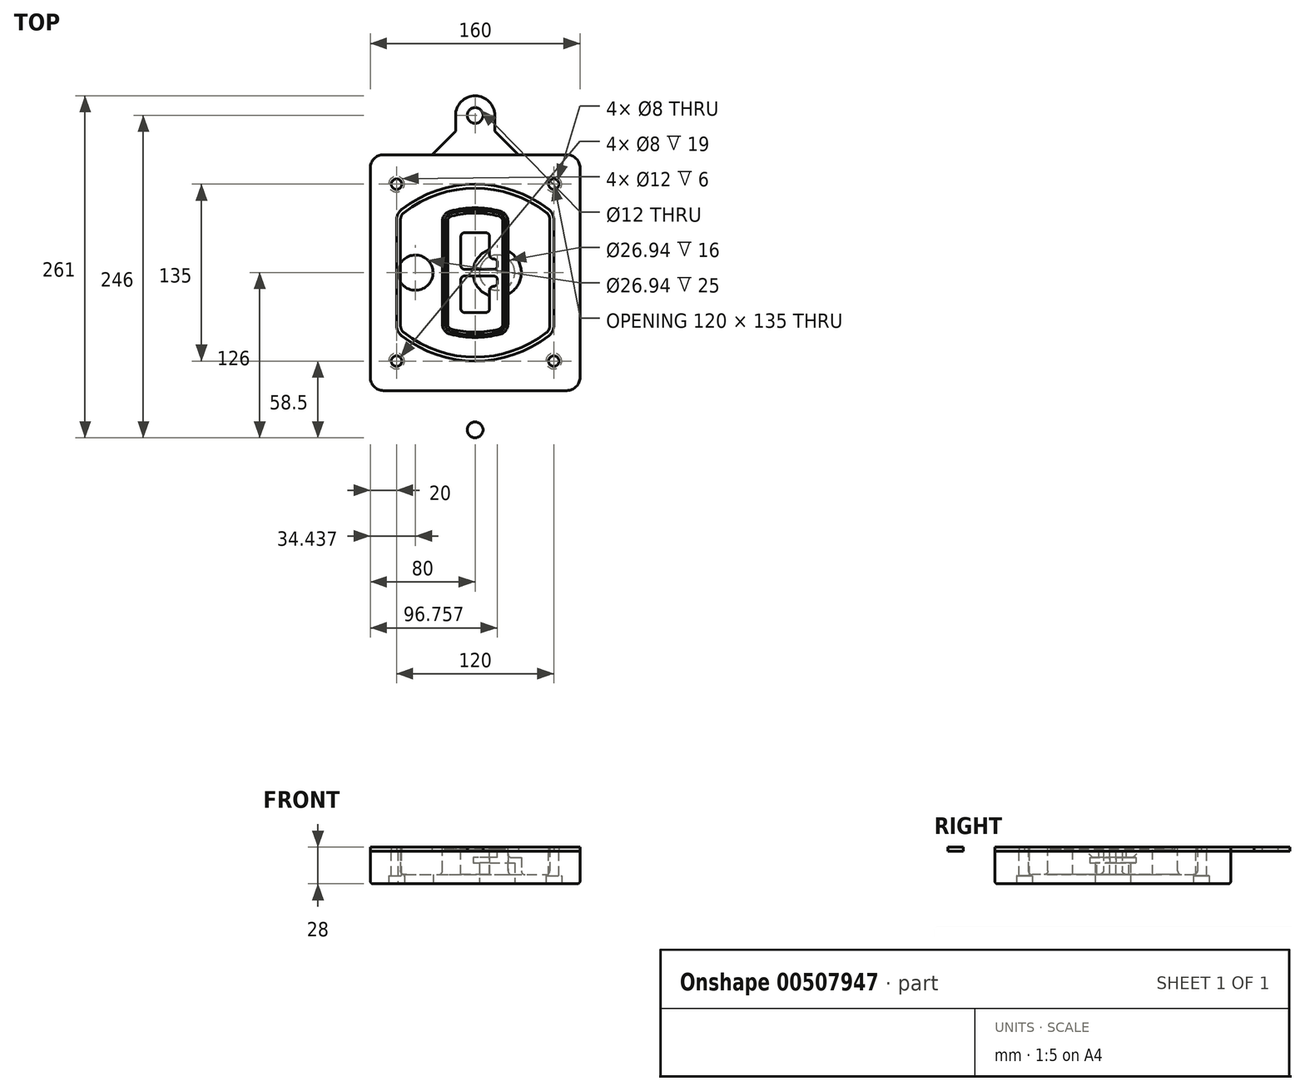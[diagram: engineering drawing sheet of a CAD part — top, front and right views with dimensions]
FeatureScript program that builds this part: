
annotation { "Feature Type Name" : "Feature", "Feature Type Description" : "" }
export const myFeature = defineFeature(function(context is Context, id is Id, definition is map)
    precondition{}
    {
        {
            var Q0;
            Q0=qCreatedBy(makeId("Top.planeOp"),FACE);
            var sketch = newSketch(context, id + "F0", { "sketchPlane" : qUnion([Q0])});
            skPoint(sketch, "E0.rect.middle", {"position": v(0, 0) * mm});
            skLineSegment(sketch, "E1.bottom", {"start": v(-70, -90) * mm, "end": v(70, -90) * mm});
            skLineSegment(sketch, "E1.top", {"start": v(-70, 90) * mm, "end": v(70, 90) * mm});
            skLineSegment(sketch, "E1.left", {"start": v(-80, -80) * mm, "end": v(-80, 80) * mm});
            skLineSegment(sketch, "E1.right", {"start": v(80, -80) * mm, "end": v(80, 80) * mm});
            skLineSegment(sketch, "E2", {"start": v(-80, 90) * mm, "end": v(80, -90) * mm, "construction": true});
            skLineSegment(sketch, "E3", {"start": v(80, 90) * mm, "end": v(-80, -90) * mm, "construction": true});
            skCircle(sketch, "E4", {"center": v(-60, 67.5) * mm, "radius": 4 * mm});
            skCircle(sketch, "E5", {"center": v(60, 67.5) * mm, "radius": 4 * mm});
            skCircle(sketch, "E6", {"center": v(60, -67.5) * mm, "radius": 4 * mm});
            skCircle(sketch, "E7", {"center": v(-60, -67.5) * mm, "radius": 4 * mm});
            skLineSegment(sketch, "E8", {"start": v(-60, 67.5) * mm, "end": v(60, 67.5) * mm, "construction": true});
            skLineSegment(sketch, "E9", {"start": v(60, 67.5) * mm, "end": v(60, -67.5) * mm, "construction": true});
            skLineSegment(sketch, "E10", {"start": v(60, -67.5) * mm, "end": v(-60, -67.5) * mm, "construction": true});
            skLineSegment(sketch, "E11", {"start": v(-60, -67.5) * mm, "end": v(-60, 67.5) * mm, "construction": true});
            skLineSegment(sketch, "E12", {"start": v(-60, 40.3) * mm, "end": v(-60, -40.3) * mm});
            skLineSegment(sketch, "E13", {"start": v(60, 40.3) * mm, "end": v(60, -40.3) * mm});
            skArc(sketch, "E14", {"start": v(56.15, 48.18) * mm, "mid": v(0, 67.5) * mm, "end": v(-56.15, 48.18) * mm});
            skArc(sketch, "E15", {"start": v(-56.15, -48.18) * mm, "mid": v(0, -67.5) * mm, "end": v(56.15, -48.18) * mm});
            skLineSegment(sketch, "E16", {"start": v(-60, 0) * mm, "end": v(60, 0) * mm, "construction": true});
            skPoint(sketch, "E17.visualSharp", {"position": v(-60, -45) * mm});
            skArc(sketch, "E17.filletArc", {"start": v(-60, -40.3) * mm, "mid": v(-58.99, -44.68) * mm, "end": v(-56.15, -48.18) * mm});
            skPoint(sketch, "E18.visualSharp", {"position": v(-60, 45) * mm});
            skArc(sketch, "E18.filletArc", {"start": v(-56.15, 48.18) * mm, "mid": v(-58.99, 44.68) * mm, "end": v(-60, 40.3) * mm});
            skPoint(sketch, "E19.visualSharp", {"position": v(60, 45) * mm});
            skArc(sketch, "E19.filletArc", {"start": v(60, 40.3) * mm, "mid": v(58.99, 44.68) * mm, "end": v(56.15, 48.18) * mm});
            skPoint(sketch, "E20.visualSharp", {"position": v(60, -45) * mm});
            skArc(sketch, "E20.filletArc", {"start": v(56.15, -48.18) * mm, "mid": v(58.99, -44.68) * mm, "end": v(60, -40.3) * mm});
            skPoint(sketch, "E21.visualSharp", {"position": v(-80, 90) * mm});
            skArc(sketch, "E21.filletArc", {"start": v(-70, 90) * mm, "mid": v(-77.07, 87.07) * mm, "end": v(-80, 80) * mm});
            skPoint(sketch, "E22.visualSharp", {"position": v(80, 90) * mm});
            skArc(sketch, "E22.filletArc", {"start": v(80, 80) * mm, "mid": v(77.07, 87.07) * mm, "end": v(70, 90) * mm});
            skPoint(sketch, "E23.visualSharp", {"position": v(80, -90) * mm});
            skArc(sketch, "E23.filletArc", {"start": v(70, -90) * mm, "mid": v(77.07, -87.07) * mm, "end": v(80, -80) * mm});
            skPoint(sketch, "E24.visualSharp", {"position": v(-80, -90) * mm});
            skArc(sketch, "E24.filletArc", {"start": v(-80, -80) * mm, "mid": v(-77.07, -87.07) * mm, "end": v(-70, -90) * mm});
            skArc(sketch, "E25.0", {"start": v(57, 40.3) * mm, "mid": v(56.3, 43.36) * mm, "end": v(54.3, 45.81) * mm});
            skLineSegment(sketch, "E25.1", {"start": v(57, 40.3) * mm, "end": v(57, -40.3) * mm});
            skArc(sketch, "E25.2", {"start": v(54.3, -45.81) * mm, "mid": v(56.3, -43.36) * mm, "end": v(57, -40.3) * mm});
            skArc(sketch, "E25.3", {"start": v(-54.3, -45.81) * mm, "mid": v(0, -64.5) * mm, "end": v(54.3, -45.81) * mm});
            skArc(sketch, "E25.4", {"start": v(-57, -40.3) * mm, "mid": v(-56.3, -43.36) * mm, "end": v(-54.3, -45.81) * mm});
            skArc(sketch, "E25.5", {"start": v(54.3, 45.81) * mm, "mid": v(0, 64.5) * mm, "end": v(-54.3, 45.81) * mm});
            skLineSegment(sketch, "E25.6", {"start": v(-57, 40.3) * mm, "end": v(-57, -40.3) * mm});
            skArc(sketch, "E25.7", {"start": v(-54.3, 45.81) * mm, "mid": v(-56.3, 43.36) * mm, "end": v(-57, 40.3) * mm});
            skArc(sketch, "E26.0", {"start": v(-58.62, 51.33) * mm, "mid": v(-62.58, 46.43) * mm, "end": v(-64, 40.3) * mm});
            skArc(sketch, "E26.1", {"start": v(58.62, 51.33) * mm, "mid": v(0, 71.5) * mm, "end": v(-58.62, 51.33) * mm});
            skArc(sketch, "E26.2", {"start": v(64, 40.3) * mm, "mid": v(62.58, 46.43) * mm, "end": v(58.62, 51.33) * mm});
            skLineSegment(sketch, "E26.3", {"start": v(64, 40.3) * mm, "end": v(64, -40.3) * mm});
            skArc(sketch, "E26.4", {"start": v(58.62, -51.33) * mm, "mid": v(62.58, -46.43) * mm, "end": v(64, -40.3) * mm});
            skLineSegment(sketch, "E26.5", {"start": v(-64, 40.3) * mm, "end": v(-64, -40.3) * mm});
            skArc(sketch, "E26.6", {"start": v(-58.62, -51.33) * mm, "mid": v(0, -71.5) * mm, "end": v(58.62, -51.33) * mm});
            skArc(sketch, "E26.7", {"start": v(-64, -40.3) * mm, "mid": v(-62.58, -46.43) * mm, "end": v(-58.62, -51.33) * mm});
            skSolve(sketch);
        }
        {
            var Q0;
            Q0=makeQuery(id+"F0.imprint","IMPRINT",FACE,{"disambiguationData":[TD([[makeQuery(id+"F0.imprint","IMPRINT",EDGE,{"derivedFrom":sQuery(id+"F0.wireOp",EDGE,"E1.bottom")}),1.0]])]});
            var Q1;
            Q1=makeQuery(id+"F0.imprint","IMPRINT",FACE,{"disambiguationData":[TD([[makeQuery(id+"F0.imprint","IMPRINT",EDGE,{"derivedFrom":sQuery(id+"F0.wireOp",EDGE,"E12")}),1.0]])]});
            var Q2;
            Q2=makeQuery(id+"F0.imprint","IMPRINT",FACE,{"disambiguationData":[TD([[makeQuery(id+"F0.imprint","IMPRINT",EDGE,{"derivedFrom":sQuery(id+"F0.wireOp",EDGE,"E25.0")}),1.0]])]});
            var Q3;
            Q3=makeQuery(id+"F0.imprint","IMPRINT",FACE,{"disambiguationData":[TD([[makeQuery(id+"F0.imprint","IMPRINT",EDGE,{"derivedFrom":sQuery(id+"F0.wireOp",EDGE,"E12")}),-1.0]])]});
            extrude(context, id + "F1", {"entities" : qUnion([Q0, Q1, Q2, Q3]), "oppositeDirection" : true, "depth" : 25 * mm});
        }
        {
            var Q0;
            Q0=makeQuery(id+"F0.imprint","IMPRINT",FACE,{"disambiguationData":[TD([[makeQuery(id+"F0.imprint","IMPRINT",EDGE,{"derivedFrom":sQuery(id+"F0.wireOp",EDGE,"E12")}),1.0]])]});
            extrude(context, id + "F2", {"entities" : qUnion([Q0]), "operationType" : NewBodyOperationType.ADD, "depth" : 3 * mm});
        }
        {
            var Q0;
            Q0=makeQuery(id+"F0.imprint","IMPRINT",FACE,{"disambiguationData":[TD([[makeQuery(id+"F0.imprint","IMPRINT",EDGE,{"derivedFrom":sQuery(id+"F0.wireOp",EDGE,"E25.0")}),1.0]])]});
            extrude(context, id + "F3", {"entities" : qUnion([Q0]), "operationType" : NewBodyOperationType.REMOVE, "oppositeDirection" : true, "depth" : 18 * mm});
        }
        {
            var Q0;
            Q0=makeQuery(id+"F2.opExtrude","CAP_FACE",FACE,{"disambiguationData":[OSD([sQuery(id+"F0.wireOp",EDGE,"E12"),sQuery(id+"F0.wireOp",EDGE,"E13"),sQuery(id+"F0.wireOp",EDGE,"E14"),sQuery(id+"F0.wireOp",EDGE,"E15"),sQuery(id+"F0.wireOp",EDGE,"E17.filletArc"),sQuery(id+"F0.wireOp",EDGE,"E18.filletArc"),sQuery(id+"F0.wireOp",EDGE,"E19.filletArc"),sQuery(id+"F0.wireOp",EDGE,"E20.filletArc"),sQuery(id+"F0.wireOp",EDGE,"E25.0"),sQuery(id+"F0.wireOp",EDGE,"E25.1"),sQuery(id+"F0.wireOp",EDGE,"E25.2"),sQuery(id+"F0.wireOp",EDGE,"E25.3"),sQuery(id+"F0.wireOp",EDGE,"E25.4"),sQuery(id+"F0.wireOp",EDGE,"E25.5"),sQuery(id+"F0.wireOp",EDGE,"E25.6"),sQuery(id+"F0.wireOp",EDGE,"E25.7")])],"isStart":false});
            var sketch = newSketch(context, id + "F4", { "sketchPlane" : qUnion([Q0])});
            skArc(sketch, "E27.0", {"start": v(-19.08, -46.97) * mm, "mid": v(0, -49.5) * mm, "end": v(19.08, -46.97) * mm});
            skArc(sketch, "E28.0", {"start": v(19.08, 46.97) * mm, "mid": v(0, 49.5) * mm, "end": v(-19.08, 46.97) * mm});
            skLineSegment(sketch, "E29", {"start": v(-25, 39.25) * mm, "end": v(-25, -39.25) * mm});
            skLineSegment(sketch, "E30", {"start": v(25, 39.25) * mm, "end": v(25, -39.25) * mm});
            skLineSegment(sketch, "E31", {"start": v(-25, 45.1) * mm, "end": v(25, 45.1) * mm, "construction": true});
            skLineSegment(sketch, "E32", {"start": v(-25, -45.1) * mm, "end": v(25, -45.1) * mm, "construction": true});
            skPoint(sketch, "E33.visualSharp", {"position": v(-25, 45.1) * mm});
            skArc(sketch, "E33.filletArc", {"start": v(-19.08, 46.97) * mm, "mid": v(-23.35, 44.11) * mm, "end": v(-25, 39.25) * mm});
            skPoint(sketch, "E34.visualSharp", {"position": v(25, 45.1) * mm});
            skArc(sketch, "E34.filletArc", {"start": v(25, 39.25) * mm, "mid": v(23.35, 44.11) * mm, "end": v(19.08, 46.97) * mm});
            skPoint(sketch, "E35.visualSharp", {"position": v(25, -45.1) * mm});
            skArc(sketch, "E35.filletArc", {"start": v(19.08, -46.97) * mm, "mid": v(23.35, -44.11) * mm, "end": v(25, -39.25) * mm});
            skPoint(sketch, "E36.visualSharp", {"position": v(-25, -45.1) * mm});
            skArc(sketch, "E36.filletArc", {"start": v(-25, -39.25) * mm, "mid": v(-23.35, -44.11) * mm, "end": v(-19.08, -46.97) * mm});
            skArc(sketch, "E37.0", {"start": v(54.3, 45.81) * mm, "mid": v(0, 64.5) * mm, "end": v(-54.3, 45.81) * mm});
            skArc(sketch, "E37.1", {"start": v(-54.3, 45.81) * mm, "mid": v(-56.3, 43.36) * mm, "end": v(-57, 40.3) * mm});
            skLineSegment(sketch, "E37.2", {"start": v(-57, 40.3) * mm, "end": v(-57, -40.3) * mm});
            skArc(sketch, "E37.3", {"start": v(-57, -40.3) * mm, "mid": v(-56.3, -43.36) * mm, "end": v(-54.3, -45.81) * mm});
            skArc(sketch, "E37.4", {"start": v(-54.3, -45.81) * mm, "mid": v(0, -64.5) * mm, "end": v(54.3, -45.81) * mm});
            skArc(sketch, "E37.5", {"start": v(54.3, -45.81) * mm, "mid": v(56.3, -43.36) * mm, "end": v(57, -40.3) * mm});
            skLineSegment(sketch, "E37.6", {"start": v(57, 40.3) * mm, "end": v(57, -40.3) * mm});
            skArc(sketch, "E37.7", {"start": v(57, 40.3) * mm, "mid": v(56.3, 43.36) * mm, "end": v(54.3, 45.81) * mm});
            skLineSegment(sketch, "E38.0", {"start": v(23, 39.25) * mm, "end": v(23, -39.25) * mm});
            skArc(sketch, "E38.1", {"start": v(18.56, -45.04) * mm, "mid": v(21.76, -42.9) * mm, "end": v(23, -39.25) * mm});
            skArc(sketch, "E38.2", {"start": v(-18.56, -45.04) * mm, "mid": v(0, -47.5) * mm, "end": v(18.56, -45.04) * mm});
            skArc(sketch, "E38.3", {"start": v(-23, -39.25) * mm, "mid": v(-21.76, -42.9) * mm, "end": v(-18.56, -45.04) * mm});
            skLineSegment(sketch, "E38.4", {"start": v(-23, 39.25) * mm, "end": v(-23, -39.25) * mm});
            skArc(sketch, "E38.5", {"start": v(23, 39.25) * mm, "mid": v(21.76, 42.9) * mm, "end": v(18.56, 45.04) * mm});
            skArc(sketch, "E38.6", {"start": v(-18.56, 45.04) * mm, "mid": v(-21.76, 42.9) * mm, "end": v(-23, 39.25) * mm});
            skArc(sketch, "E38.7", {"start": v(18.56, 45.04) * mm, "mid": v(0, 47.5) * mm, "end": v(-18.56, 45.04) * mm});
            skArc(sketch, "E39.0", {"start": v(21, 39.25) * mm, "mid": v(20.18, 41.68) * mm, "end": v(18.04, 43.1) * mm});
            skLineSegment(sketch, "E39.1", {"start": v(21, 39.25) * mm, "end": v(21, -39.25) * mm});
            skArc(sketch, "E39.2", {"start": v(18.04, -43.1) * mm, "mid": v(20.18, -41.68) * mm, "end": v(21, -39.25) * mm});
            skArc(sketch, "E39.3", {"start": v(-18.04, -43.1) * mm, "mid": v(0, -45.5) * mm, "end": v(18.04, -43.1) * mm});
            skArc(sketch, "E39.4", {"start": v(-21, -39.25) * mm, "mid": v(-20.18, -41.68) * mm, "end": v(-18.04, -43.1) * mm});
            skArc(sketch, "E39.5", {"start": v(18.04, 43.1) * mm, "mid": v(0, 45.5) * mm, "end": v(-18.04, 43.1) * mm});
            skLineSegment(sketch, "E39.6", {"start": v(-21, 39.25) * mm, "end": v(-21, -39.25) * mm});
            skArc(sketch, "E39.7", {"start": v(-18.04, 43.1) * mm, "mid": v(-20.18, 41.68) * mm, "end": v(-21, 39.25) * mm});
            skLineSegment(sketch, "E40", {"start": v(-25, 0) * mm, "end": v(25, 0) * mm, "construction": true});
            skLineSegment(sketch, "E41", {"start": v(-11, 5.5) * mm, "end": v(-11, 27.5) * mm});
            skLineSegment(sketch, "E42", {"start": v(-8, 30.5) * mm, "end": v(8, 30.5) * mm});
            skLineSegment(sketch, "E43", {"start": v(11, 27.5) * mm, "end": v(11, 13.5) * mm});
            skLineSegment(sketch, "E44", {"start": v(14, 10.5) * mm, "end": v(14, 10.5) * mm});
            skLineSegment(sketch, "E45", {"start": v(17, 7.5) * mm, "end": v(17, 5.5) * mm});
            skLineSegment(sketch, "E46", {"start": v(14, 2.5) * mm, "end": v(-8, 2.5) * mm});
            skPoint(sketch, "E47.visualSharp", {"position": v(-11, 30.5) * mm});
            skArc(sketch, "E47.filletArc", {"start": v(-8, 30.5) * mm, "mid": v(-10.12, 29.62) * mm, "end": v(-11, 27.5) * mm});
            skPoint(sketch, "E48.visualSharp", {"position": v(11, 30.5) * mm});
            skArc(sketch, "E48.filletArc", {"start": v(11, 27.5) * mm, "mid": v(10.12, 29.62) * mm, "end": v(8, 30.5) * mm});
            skPoint(sketch, "E49.visualSharp", {"position": v(11, 10.5) * mm});
            skArc(sketch, "E49.filletArc", {"start": v(11, 13.5) * mm, "mid": v(11.88, 11.38) * mm, "end": v(14, 10.5) * mm});
            skPoint(sketch, "E50.visualSharp", {"position": v(17, 10.5) * mm});
            skArc(sketch, "E50.filletArc", {"start": v(17, 7.5) * mm, "mid": v(16.12, 9.62) * mm, "end": v(14, 10.5) * mm});
            skPoint(sketch, "E51.visualSharp", {"position": v(17, 2.5) * mm});
            skArc(sketch, "E51.filletArc", {"start": v(14, 2.5) * mm, "mid": v(16.12, 3.38) * mm, "end": v(17, 5.5) * mm});
            skPoint(sketch, "E52.visualSharp", {"position": v(-11, 2.5) * mm});
            skArc(sketch, "E52.filletArc", {"start": v(-11, 5.5) * mm, "mid": v(-10.12, 3.38) * mm, "end": v(-8, 2.5) * mm});
            skLineSegment(sketch, "E53.0.MirrorCS", {"start": v(14, -2.5) * mm, "end": v(-8, -2.5) * mm});
            skArc(sketch, "E54.0.MirrorCS", {"start": v(-11, -5.5) * mm, "mid": v(-10.12, -3.38) * mm, "end": v(-8, -2.5) * mm});
            skLineSegment(sketch, "E55.0.MirrorCS", {"start": v(-11, -5.5) * mm, "end": v(-11, -27.5) * mm});
            skArc(sketch, "E56.0.MirrorCS", {"start": v(-8, -30.5) * mm, "mid": v(-10.12, -29.62) * mm, "end": v(-11, -27.5) * mm});
            skLineSegment(sketch, "E57.0.MirrorCS", {"start": v(-8, -30.5) * mm, "end": v(8, -30.5) * mm});
            skArc(sketch, "E58.0.MirrorCS", {"start": v(11, -27.5) * mm, "mid": v(10.12, -29.62) * mm, "end": v(8, -30.5) * mm});
            skLineSegment(sketch, "E59.0.MirrorCS", {"start": v(11, -27.5) * mm, "end": v(11, -13.5) * mm});
            skArc(sketch, "E60.0.MirrorCS", {"start": v(11, -13.5) * mm, "mid": v(11.88, -11.38) * mm, "end": v(14, -10.5) * mm});
            skArc(sketch, "E61.0.MirrorCS", {"start": v(17, -7.5) * mm, "mid": v(16.12, -9.62) * mm, "end": v(14, -10.5) * mm});
            skLineSegment(sketch, "E62.0.MirrorCS", {"start": v(17, -7.5) * mm, "end": v(17, -5.5) * mm});
            skArc(sketch, "E63.0.MirrorCS", {"start": v(14, -2.5) * mm, "mid": v(16.12, -3.38) * mm, "end": v(17, -5.5) * mm});
            skSolve(sketch);
        }
        {
            var Q0;
            Q0=makeQuery(id+"F4.imprint","IMPRINT",FACE,{"disambiguationData":[TD([[makeQuery(id+"F4.imprint","IMPRINT",EDGE,{"derivedFrom":sQuery(id+"F4.wireOp",EDGE,"E27.0")}),1.0]])]});
            var Q1;
            Q1=makeQuery(id+"F4.imprint","IMPRINT",FACE,{"disambiguationData":[TD([[makeQuery(id+"F4.imprint","IMPRINT",EDGE,{"derivedFrom":sQuery(id+"F4.wireOp",EDGE,"E38.0")}),-1.0]])]});
            var Q2;
            Q2=makeQuery(id+"F4.imprint","IMPRINT",FACE,{"disambiguationData":[TD([[makeQuery(id+"F4.imprint","IMPRINT",EDGE,{"derivedFrom":sQuery(id+"F4.wireOp",EDGE,"E39.0")}),1.0]])]});
            extrude(context, id + "F5", {"entities" : qUnion([Q0, Q1, Q2]), "operationType" : NewBodyOperationType.ADD, "endBound" : BoundingType.UP_TO_NEXT, "oppositeDirection" : true, "depth" : 25 * mm});
        }
        {
            var Q0;
            Q0=makeQuery(id+"F4.imprint","IMPRINT",FACE,{"disambiguationData":[TD([[makeQuery(id+"F4.imprint","IMPRINT",EDGE,{"derivedFrom":sQuery(id+"F4.wireOp",EDGE,"E38.0")}),-1.0]])]});
            extrude(context, id + "F6", {"entities" : qUnion([Q0]), "operationType" : NewBodyOperationType.REMOVE, "oppositeDirection" : true, "depth" : 2 * mm});
        }
        {
            var Q0;
            Q0=makeQuery(id+"F1.opExtrude","CAP_FACE",FACE,{"disambiguationData":[OSD([sQuery(id+"F0.wireOp",EDGE,"E1.bottom"),sQuery(id+"F0.wireOp",EDGE,"E1.top"),sQuery(id+"F0.wireOp",EDGE,"E1.left"),sQuery(id+"F0.wireOp",EDGE,"E1.right"),sQuery(id+"F0.wireOp",EDGE,"E4"),sQuery(id+"F0.wireOp",EDGE,"E5"),sQuery(id+"F0.wireOp",EDGE,"E6"),sQuery(id+"F0.wireOp",EDGE,"E7"),sQuery(id+"F0.wireOp",EDGE,"E21.filletArc"),sQuery(id+"F0.wireOp",EDGE,"E22.filletArc"),sQuery(id+"F0.wireOp",EDGE,"E23.filletArc"),sQuery(id+"F0.wireOp",EDGE,"E24.filletArc")])],"isStart":false});
            var sketch = newSketch(context, id + "F7", { "sketchPlane" : qUnion([Q0])});
            skCircle(sketch, "E64", {"center": v(16.76, 0) * mm, "radius": 13.47 * mm});
            skCircle(sketch, "E65", {"center": v(-45.56, 0) * mm, "radius": 13.47 * mm});
            skLineSegment(sketch, "E66", {"start": v(80, 0) * mm, "end": v(-80, 0) * mm});
            skCircle(sketch, "E67", {"center": v(16.76, 0) * mm, "radius": 18.47 * mm});
            skCircle(sketch, "E68", {"center": v(60, -67.5) * mm, "radius": 6 * mm});
            skCircle(sketch, "E69", {"center": v(-60, -67.5) * mm, "radius": 6 * mm});
            skCircle(sketch, "E70", {"center": v(-60, 67.5) * mm, "radius": 6 * mm});
            skCircle(sketch, "E71", {"center": v(60, 67.5) * mm, "radius": 6 * mm});
            skSolve(sketch);
        }
        {
            var Q0;
            {var subQ1=sQuery(id+"F7.wireOp",EDGE,"E66");var subQ4=sQuery(id+"F7.wireOp",EDGE,"E64");var subQ6=makeQuery(id+"F7.imprint","INTERSECT",VERTEX,{"disambiguationData":[OD(0.0)],"derivedFrom":[subQ4,subQ1]});Q0=makeQuery(id+"F7.imprint","IMPRINT",FACE,{"disambiguationData":[TD([[makeQuery(id+"F7.imprint","IMPRINT",EDGE,{"disambiguationData":[TD([[subQ6,-1.0]])],"derivedFrom":subQ4}),-1.0]])]});}
            var Q1;
            {var subQ0=sQuery(id+"F7.wireOp",EDGE,"E66");var subQ1=sQuery(id+"F7.wireOp",EDGE,"E64");var subQ3=makeQuery(id+"F7.imprint","INTERSECT",VERTEX,{"disambiguationData":[OD(0.0)],"derivedFrom":[subQ1,subQ0]});Q1=makeQuery(id+"F7.imprint","IMPRINT",FACE,{"disambiguationData":[TD([[makeQuery(id+"F7.imprint","IMPRINT",EDGE,{"disambiguationData":[TD([[subQ3,-1.0]])],"derivedFrom":subQ1}),1.0]])]});}
            var Q2;
            {var subQ0=sQuery(id+"F7.wireOp",EDGE,"E66");var subQ1=sQuery(id+"F7.wireOp",EDGE,"E64");var subQ3=makeQuery(id+"F7.imprint","INTERSECT",VERTEX,{"disambiguationData":[OD(0.0)],"derivedFrom":[subQ1,subQ0]});Q2=makeQuery(id+"F7.imprint","IMPRINT",FACE,{"disambiguationData":[TD([[makeQuery(id+"F7.imprint","IMPRINT",EDGE,{"disambiguationData":[TD([[subQ3,1.0]])],"derivedFrom":subQ1}),1.0]])]});}
            var Q3;
            {var subQ1=sQuery(id+"F7.wireOp",EDGE,"E66");var subQ4=sQuery(id+"F7.wireOp",EDGE,"E64");var subQ6=makeQuery(id+"F7.imprint","INTERSECT",VERTEX,{"disambiguationData":[OD(0.0)],"derivedFrom":[subQ4,subQ1]});Q3=makeQuery(id+"F7.imprint","IMPRINT",FACE,{"disambiguationData":[TD([[makeQuery(id+"F7.imprint","IMPRINT",EDGE,{"disambiguationData":[TD([[subQ6,1.0]])],"derivedFrom":subQ4}),-1.0]])]});}
            extrude(context, id + "F8", {"entities" : qUnion([Q0, Q1, Q2, Q3]), "operationType" : NewBodyOperationType.ADD, "oppositeDirection" : true, "depth" : 20 * mm});
        }
        {
            var Q0;
            {var subQ0=sQuery(id+"F7.wireOp",EDGE,"E66");var subQ1=sQuery(id+"F7.wireOp",EDGE,"E64");var subQ3=makeQuery(id+"F7.imprint","INTERSECT",VERTEX,{"disambiguationData":[OD(0.0)],"derivedFrom":[subQ1,subQ0]});Q0=makeQuery(id+"F7.imprint","IMPRINT",FACE,{"disambiguationData":[TD([[makeQuery(id+"F7.imprint","IMPRINT",EDGE,{"disambiguationData":[TD([[subQ3,-1.0]])],"derivedFrom":subQ1}),1.0]])]});}
            var Q1;
            {var subQ0=sQuery(id+"F7.wireOp",EDGE,"E66");var subQ1=sQuery(id+"F7.wireOp",EDGE,"E64");var subQ3=makeQuery(id+"F7.imprint","INTERSECT",VERTEX,{"disambiguationData":[OD(0.0)],"derivedFrom":[subQ1,subQ0]});Q1=makeQuery(id+"F7.imprint","IMPRINT",FACE,{"disambiguationData":[TD([[makeQuery(id+"F7.imprint","IMPRINT",EDGE,{"disambiguationData":[TD([[subQ3,1.0]])],"derivedFrom":subQ1}),1.0]])]});}
            extrude(context, id + "F9", {"entities" : qUnion([Q0, Q1]), "operationType" : NewBodyOperationType.REMOVE, "oppositeDirection" : true, "depth" : 16 * mm});
        }
        {
            var Q0;
            {var subQ0=sQuery(id+"F7.wireOp",EDGE,"E66");var subQ1=sQuery(id+"F7.wireOp",EDGE,"E65");var subQ3=makeQuery(id+"F7.imprint","INTERSECT",VERTEX,{"disambiguationData":[OD(0.0)],"derivedFrom":[subQ1,subQ0]});Q0=makeQuery(id+"F7.imprint","IMPRINT",FACE,{"disambiguationData":[TD([[makeQuery(id+"F7.imprint","IMPRINT",EDGE,{"disambiguationData":[TD([[subQ3,-1.0]])],"derivedFrom":subQ1}),1.0]])]});}
            var Q1;
            {var subQ0=sQuery(id+"F7.wireOp",EDGE,"E66");var subQ1=sQuery(id+"F7.wireOp",EDGE,"E65");var subQ3=makeQuery(id+"F7.imprint","INTERSECT",VERTEX,{"disambiguationData":[OD(0.0)],"derivedFrom":[subQ1,subQ0]});Q1=makeQuery(id+"F7.imprint","IMPRINT",FACE,{"disambiguationData":[TD([[makeQuery(id+"F7.imprint","IMPRINT",EDGE,{"disambiguationData":[TD([[subQ3,1.0]])],"derivedFrom":subQ1}),1.0]])]});}
            extrude(context, id + "F10", {"entities" : qUnion([Q0, Q1]), "operationType" : NewBodyOperationType.REMOVE, "oppositeDirection" : true, "depth" : 25 * mm});
        }
        {
            var Q0;
            Q0=makeQuery(id+"F7.imprint","IMPRINT",FACE,{"disambiguationData":[TD([[makeQuery(id+"F7.imprint","IMPRINT",EDGE,{"derivedFrom":sQuery(id+"F7.wireOp",EDGE,"E68")}),1.0]])]});
            var Q1;
            Q1=makeQuery(id+"F7.imprint","IMPRINT",FACE,{"disambiguationData":[TD([[makeQuery(id+"F7.imprint","IMPRINT",EDGE,{"derivedFrom":makeQuery(id+"F1.opExtrude","CAP_EDGE",EDGE,{"disambiguationData":[OSD([sQuery(id+"F0.wireOp",EDGE,"E5")])],"isStart":false})}),-1.0]])]});
            var Q2;
            Q2=makeQuery(id+"F7.imprint","IMPRINT",FACE,{"disambiguationData":[TD([[makeQuery(id+"F7.imprint","IMPRINT",EDGE,{"derivedFrom":sQuery(id+"F7.wireOp",EDGE,"E69")}),1.0]])]});
            var Q3;
            Q3=makeQuery(id+"F7.imprint","IMPRINT",FACE,{"disambiguationData":[TD([[makeQuery(id+"F7.imprint","IMPRINT",EDGE,{"derivedFrom":makeQuery(id+"F1.opExtrude","CAP_EDGE",EDGE,{"disambiguationData":[OSD([sQuery(id+"F0.wireOp",EDGE,"E4")])],"isStart":false})}),-1.0]])]});
            var Q4;
            Q4=makeQuery(id+"F7.imprint","IMPRINT",FACE,{"disambiguationData":[TD([[makeQuery(id+"F7.imprint","IMPRINT",EDGE,{"derivedFrom":sQuery(id+"F7.wireOp",EDGE,"E70")}),1.0]])]});
            var Q5;
            Q5=makeQuery(id+"F7.imprint","IMPRINT",FACE,{"disambiguationData":[TD([[makeQuery(id+"F7.imprint","IMPRINT",EDGE,{"derivedFrom":makeQuery(id+"F1.opExtrude","CAP_EDGE",EDGE,{"disambiguationData":[OSD([sQuery(id+"F0.wireOp",EDGE,"E7")])],"isStart":false})}),-1.0]])]});
            var Q6;
            Q6=makeQuery(id+"F7.imprint","IMPRINT",FACE,{"disambiguationData":[TD([[makeQuery(id+"F7.imprint","IMPRINT",EDGE,{"derivedFrom":sQuery(id+"F7.wireOp",EDGE,"E71")}),1.0]])]});
            var Q7;
            Q7=makeQuery(id+"F7.imprint","IMPRINT",FACE,{"disambiguationData":[TD([[makeQuery(id+"F7.imprint","IMPRINT",EDGE,{"derivedFrom":makeQuery(id+"F1.opExtrude","CAP_EDGE",EDGE,{"disambiguationData":[OSD([sQuery(id+"F0.wireOp",EDGE,"E6")])],"isStart":false})}),-1.0]])]});
            extrude(context, id + "F11", {"entities" : qUnion([Q0, Q1, Q2, Q3, Q4, Q5, Q6, Q7]), "operationType" : NewBodyOperationType.REMOVE, "oppositeDirection" : true, "depth" : 6 * mm});
        }
        {
            var Q0;
            Q0=makeQuery(id+"F9.boolean.opBoolean","COPY",FACE,{"derivedFrom":makeQuery(id+"F9.opExtrude","CAP_FACE",FACE,{"disambiguationData":[OSD([sQuery(id+"F7.wireOp",EDGE,"E64")])],"isStart":false})});
            var sketch = newSketch(context, id + "F12", { "sketchPlane" : qUnion([Q0])});
            skArc(sketch, "E72.0", {"start": v(11, 17.55) * mm, "mid": v(2.57, 11.82) * mm, "end": v(-1.54, 2.5) * mm});
            skArc(sketch, "E72.1", {"start": v(-1.54, -2.5) * mm, "mid": v(2.57, -11.82) * mm, "end": v(11, -17.55) * mm});
            skLineSegment(sketch, "E73", {"start": v(-1.54, -2.5) * mm, "end": v(14, -2.5) * mm});
            skLineSegment(sketch, "E74.0", {"start": v(14, 2.5) * mm, "end": v(-1.54, 2.5) * mm});
            skArc(sketch, "E74.1", {"start": v(14, 2.5) * mm, "mid": v(16.12, 3.38) * mm, "end": v(17, 5.5) * mm});
            skLineSegment(sketch, "E74.2", {"start": v(17, 7.5) * mm, "end": v(17, 5.5) * mm});
            skArc(sketch, "E74.3", {"start": v(17, 7.5) * mm, "mid": v(16.12, 9.62) * mm, "end": v(14, 10.5) * mm});
            skArc(sketch, "E74.4", {"start": v(11, 13.5) * mm, "mid": v(11.88, 11.38) * mm, "end": v(14, 10.5) * mm});
            skLineSegment(sketch, "E74.5", {"start": v(11, 17.55) * mm, "end": v(11, 13.5) * mm});
            skLineSegment(sketch, "E74.7", {"start": v(14, -2.5) * mm, "end": v(-1.54, -2.5) * mm});
            skArc(sketch, "E74.8", {"start": v(14, -2.5) * mm, "mid": v(16.12, -3.38) * mm, "end": v(17, -5.5) * mm});
            skLineSegment(sketch, "E74.9", {"start": v(17, -7.5) * mm, "end": v(17, -5.5) * mm});
            skArc(sketch, "E74.10", {"start": v(17, -7.5) * mm, "mid": v(16.12, -9.62) * mm, "end": v(14, -10.5) * mm});
            skArc(sketch, "E74.11", {"start": v(11, -13.5) * mm, "mid": v(11.88, -11.38) * mm, "end": v(14, -10.5) * mm});
            skLineSegment(sketch, "E74.12", {"start": v(11, -17.55) * mm, "end": v(11, -13.5) * mm});
            skPoint(sketch, "E75.orphan", {"position": v(11, -27.5) * mm});
            skPoint(sketch, "E76.orphan", {"position": v(-8, -2.5) * mm});
            skPoint(sketch, "E77.orphan", {"position": v(-8, 2.5) * mm});
            skPoint(sketch, "E78.orphan", {"position": v(11, 27.5) * mm});
            skSolve(sketch);
        }
        {
            var Q0;
            {var subQ7=sQuery(id+"F12.wireOp",EDGE,"E72.0");var subQ14=sQuery(id+"F12.wireOp",EDGE,"E72.1");var subQ16=sQuery(id+"F12.wireOp",EDGE,"E74.1");var subQ18=sQuery(id+"F12.wireOp",EDGE,"E74.8");Q0=qUnion([makeQuery(id+"F12.imprint","IMPRINT",FACE,{"disambiguationData":[TD([[makeQuery(id+"F12.imprint","IMPRINT",EDGE,{"derivedFrom":subQ7}),1.0]])]}),makeQuery(id+"F12.imprint","IMPRINT",FACE,{"disambiguationData":[TD([[makeQuery(id+"F12.imprint","IMPRINT",EDGE,{"derivedFrom":subQ14}),1.0]])]}),makeQuery(id+"F12.imprint","IMPRINT",FACE,{"disambiguationData":[TD([[makeQuery(id+"F12.imprint","IMPRINT",EDGE,{"derivedFrom":subQ16}),1.0]])]}),makeQuery(id+"F12.imprint","IMPRINT",FACE,{"disambiguationData":[TD([[makeQuery(id+"F12.imprint","IMPRINT",EDGE,{"derivedFrom":subQ18}),-1.0]])]})]);}
            var Q1;
            Q1=makeQuery(id+"F5.boolean.opBoolean","SPLIT",FACE,{"disambiguationData":[TD([makeQuery(id+"F5.opExtrude","SWEPT_FACE",FACE,{"disambiguationData":[OSD([sQuery(id+"F4.wireOp",EDGE,"E41")])]})])],"derivedFrom":makeQuery(id+"F3.boolean.opBoolean","COPY",FACE,{"derivedFrom":makeQuery(id+"F3.opExtrude","CAP_FACE",FACE,{"disambiguationData":[OSD([sQuery(id+"F0.wireOp",EDGE,"E25.0"),sQuery(id+"F0.wireOp",EDGE,"E25.1"),sQuery(id+"F0.wireOp",EDGE,"E25.2"),sQuery(id+"F0.wireOp",EDGE,"E25.3"),sQuery(id+"F0.wireOp",EDGE,"E25.4"),sQuery(id+"F0.wireOp",EDGE,"E25.5"),sQuery(id+"F0.wireOp",EDGE,"E25.6"),sQuery(id+"F0.wireOp",EDGE,"E25.7")])],"isStart":false})})});
            extrude(context, id + "F13", {"entities" : qUnion([Q0]), "operationType" : NewBodyOperationType.REMOVE, "endBound" : BoundingType.UP_TO_SURFACE, "endBoundEntityFace" : qUnion([Q1]), "depth" : 25 * mm});
        }
        {
            var Q0;
            Q0=makeQuery(id+"F3.boolean.opBoolean","COPY",EDGE,{"derivedFrom":makeQuery(id+"F3.opExtrude","CAP_EDGE",EDGE,{"disambiguationData":[OSD([sQuery(id+"F0.wireOp",EDGE,"E25.6")])],"isStart":false})});
            var Q1;
            Q1=makeQuery(id+"F8.boolean.opBoolean","INTERSECT",EDGE,{"derivedFrom":[makeQuery(id+"F5.opExtrude","SWEPT_FACE",FACE,{"disambiguationData":[OSD([sQuery(id+"F4.wireOp",EDGE,"E30")])]}),makeQuery(id+"F8.opExtrude","CAP_FACE",FACE,{"disambiguationData":[OSD([sQuery(id+"F7.wireOp",EDGE,"E67")])],"isStart":false})]});
            var Q2;
            Q2=makeQuery(id+"F8.boolean.opBoolean","INTERSECT",EDGE,{"disambiguationData":[OD(1.0)],"derivedFrom":[makeQuery(id+"F5.opExtrude","SWEPT_FACE",FACE,{"disambiguationData":[OSD([sQuery(id+"F4.wireOp",EDGE,"E30")])]}),makeQuery(id+"F8.opExtrude","SWEPT_FACE",FACE,{"disambiguationData":[OSD([sQuery(id+"F7.wireOp",EDGE,"E67")])]})]});
            var Q3;
            {var subQ0=sQuery(id+"F4.wireOp",EDGE,"E30");Q3=makeQuery(id+"F8.boolean.opBoolean","SPLIT",EDGE,{"disambiguationData":[TD([makeQuery(id+"F5.opExtrude","SWEPT_FACE",FACE,{"disambiguationData":[OSD([sQuery(id+"F4.wireOp",EDGE,"E35.filletArc")])]})])],"derivedFrom":makeQuery(id+"F5.opExtrude","CAP_EDGE",EDGE,{"disambiguationData":[OSD([subQ0])],"isStart":false})});}
            var Q4;
            {var subQ0=sQuery(id+"F0.wireOp",EDGE,"E25.7");var subQ1=sQuery(id+"F0.wireOp",EDGE,"E25.1");var subQ2=sQuery(id+"F0.wireOp",EDGE,"E25.6");var subQ3=sQuery(id+"F0.wireOp",EDGE,"E25.5");var subQ4=sQuery(id+"F0.wireOp",EDGE,"E25.4");var subQ5=sQuery(id+"F0.wireOp",EDGE,"E25.0");var subQ6=sQuery(id+"F0.wireOp",EDGE,"E25.2");var subQ7=sQuery(id+"F0.wireOp",EDGE,"E25.3");Q4=makeQuery(id+"F8.boolean.opBoolean","INTERSECT",EDGE,{"derivedFrom":[makeQuery(id+"F5.boolean.opBoolean","SPLIT",FACE,{"disambiguationData":[TD([makeQuery(id+"F2.opExtrude","SWEPT_FACE",FACE,{"disambiguationData":[OSD([subQ5])]})])],"derivedFrom":makeQuery(id+"F3.boolean.opBoolean","COPY",FACE,{"derivedFrom":makeQuery(id+"F3.opExtrude","CAP_FACE",FACE,{"disambiguationData":[OSD([subQ5,subQ1,subQ6,subQ7,subQ4,subQ3,subQ2,subQ0])],"isStart":false})})}),makeQuery(id+"F8.opExtrude","SWEPT_FACE",FACE,{"disambiguationData":[OSD([sQuery(id+"F7.wireOp",EDGE,"E67")])]})]});}
            var Q5;
            Q5=makeQuery(id+"F8.boolean.opBoolean","INTERSECT",EDGE,{"disambiguationData":[OD(0.0)],"derivedFrom":[makeQuery(id+"F5.opExtrude","SWEPT_FACE",FACE,{"disambiguationData":[OSD([sQuery(id+"F4.wireOp",EDGE,"E30")])]}),makeQuery(id+"F8.opExtrude","SWEPT_FACE",FACE,{"disambiguationData":[OSD([sQuery(id+"F7.wireOp",EDGE,"E67")])]})]});
            fillet(context, id + "F14", {"entities" : qUnion([Q0, Q1, Q2, Q3, Q4, Q5]), "radius" : 3 * mm, "tangentPropagation" : true, "allowEdgeOverflow" : false});
        }
        {
            var Q0;
            Q0=makeQuery(id+"F1.opExtrude","CAP_EDGE",EDGE,{"disambiguationData":[OSD([sQuery(id+"F0.wireOp",EDGE,"E1.bottom")])],"isStart":false});
            fillet(context, id + "F15", {"entities" : qUnion([Q0]), "radius" : 2 * mm, "tangentPropagation" : true, "allowEdgeOverflow" : false});
        }
        {
            var Q0;
            {var subQ0=sQuery(id+"F0.wireOp",EDGE,"E21.filletArc");var subQ1=sQuery(id+"F0.wireOp",EDGE,"E7");var subQ2=sQuery(id+"F0.wireOp",EDGE,"E6");var subQ3=sQuery(id+"F0.wireOp",EDGE,"E5");var subQ4=sQuery(id+"F0.wireOp",EDGE,"E4");var subQ5=sQuery(id+"F0.wireOp",EDGE,"E22.filletArc");var subQ6=sQuery(id+"F0.wireOp",EDGE,"E1.bottom");var subQ7=sQuery(id+"F0.wireOp",EDGE,"E1.right");var subQ8=sQuery(id+"F0.wireOp",EDGE,"E1.top");var subQ9=sQuery(id+"F0.wireOp",EDGE,"E1.left");var subQ10=sQuery(id+"F0.wireOp",EDGE,"E23.filletArc");var subQ11=sQuery(id+"F0.wireOp",EDGE,"E24.filletArc");Q0=makeQuery(id+"F2.boolean.opBoolean","SPLIT",FACE,{"disambiguationData":[TD([makeQuery(id+"F1.opExtrude","SWEPT_FACE",FACE,{"disambiguationData":[OSD([subQ6])]})])],"derivedFrom":makeQuery(id+"F1.opExtrude","CAP_FACE",FACE,{"disambiguationData":[OSD([subQ6,subQ8,subQ9,subQ7,subQ4,subQ3,subQ2,subQ1,subQ0,subQ5,subQ10,subQ11])],"isStart":true})});}
            var sketch = newSketch(context, id + "F16", { "sketchPlane" : qUnion([Q0])});
            skLineSegment(sketch, "E79.0", {"start": v(70, 90) * mm, "end": v(-70, 90) * mm});
            skLineSegment(sketch, "E79.1", {"start": v(-70, -90) * mm, "end": v(70, -90) * mm});
            skArc(sketch, "E79.2", {"start": v(-80, -80) * mm, "mid": v(-77.07, -87.07) * mm, "end": v(-70, -90) * mm});
            skLineSegment(sketch, "E79.3", {"start": v(-80, -80) * mm, "end": v(-80, 80) * mm});
            skLineSegment(sketch, "E79.4", {"start": v(80, -80) * mm, "end": v(80, 80) * mm});
            skArc(sketch, "E79.5", {"start": v(70, -90) * mm, "mid": v(77.07, -87.07) * mm, "end": v(80, -80) * mm});
            skArc(sketch, "E79.6", {"start": v(80, 80) * mm, "mid": v(77.07, 87.07) * mm, "end": v(70, 90) * mm});
            skArc(sketch, "E79.7", {"start": v(-70, 90) * mm, "mid": v(-77.07, 87.07) * mm, "end": v(-80, 80) * mm});
            skLineSegment(sketch, "E79.8", {"start": v(-60, 40.3) * mm, "end": v(-60, -40.3) * mm});
            skArc(sketch, "E79.9", {"start": v(56.15, 48.18) * mm, "mid": v(0, 67.5) * mm, "end": v(-56.15, 48.18) * mm});
            skArc(sketch, "E79.10", {"start": v(-56.15, -48.18) * mm, "mid": v(0, -67.5) * mm, "end": v(56.15, -48.18) * mm});
            skArc(sketch, "E79.11", {"start": v(56.15, -48.18) * mm, "mid": v(58.99, -44.68) * mm, "end": v(60, -40.3) * mm});
            skLineSegment(sketch, "E79.12", {"start": v(60, 40.3) * mm, "end": v(60, -40.3) * mm});
            skArc(sketch, "E79.13", {"start": v(-60, -40.3) * mm, "mid": v(-58.99, -44.68) * mm, "end": v(-56.15, -48.18) * mm});
            skArc(sketch, "E79.14", {"start": v(60, 40.3) * mm, "mid": v(58.99, 44.68) * mm, "end": v(56.15, 48.18) * mm});
            skArc(sketch, "E79.15", {"start": v(-56.15, 48.18) * mm, "mid": v(-58.99, 44.68) * mm, "end": v(-60, 40.3) * mm});
            skCircle(sketch, "E79.16", {"center": v(-60, 67.5) * mm, "radius": 4 * mm});
            skCircle(sketch, "E79.17", {"center": v(60, 67.5) * mm, "radius": 4 * mm});
            skCircle(sketch, "E79.18", {"center": v(60, -67.5) * mm, "radius": 4 * mm});
            skCircle(sketch, "E79.19", {"center": v(-60, -67.5) * mm, "radius": 4 * mm});
            skLineSegment(sketch, "E80", {"start": v(-33, 90) * mm, "end": v(-15, 108) * mm});
            skLineSegment(sketch, "E81", {"start": v(-15, 108) * mm, "end": v(-15, 120) * mm});
            skLineSegment(sketch, "E82", {"start": v(33, 90) * mm, "end": v(15, 108) * mm});
            skLineSegment(sketch, "E83", {"start": v(15, 108) * mm, "end": v(15, 120) * mm});
            skArc(sketch, "E84", {"start": v(15, 120) * mm, "mid": v(0, 135) * mm, "end": v(-15, 120) * mm});
            skCircle(sketch, "E85", {"center": v(0, 120) * mm, "radius": 6 * mm});
            skLineSegment(sketch, "E86", {"start": v(0, 120) * mm, "end": v(0, 90) * mm, "construction": true});
            skLineSegment(sketch, "E87", {"start": v(-80, 0) * mm, "end": v(80, 0) * mm, "construction": true});
            skCircle(sketch, "E88.MirrorC", {"center": v(0, -120) * mm, "radius": 6 * mm});
            skLineSegment(sketch, "E89.MirrorCS", {"start": v(15, -108) * mm, "end": v(15, -120) * mm});
            skLineSegment(sketch, "E90.MirrorCS", {"start": v(-15, -108) * mm, "end": v(-15, -120) * mm});
            skLineSegment(sketch, "E91.MirrorCS", {"start": v(-33, -90) * mm, "end": v(-15, -108) * mm});
            skLineSegment(sketch, "E92.MirrorCS", {"start": v(33, -90) * mm, "end": v(15, -108) * mm});
            skLineSegment(sketch, "E93.MirrorCS", {"start": v(0, -120) * mm, "end": v(0, -90) * mm, "construction": true});
            skArc(sketch, "E94.MirrorCS", {"start": v(15, -120) * mm, "mid": v(0, -135) * mm, "end": v(-15, -120) * mm});
            skSolve(sketch);
        }
        {
            var Q0;
            {var subQ0=sQuery(id+"F0.wireOp",EDGE,"E21.filletArc");var subQ1=sQuery(id+"F0.wireOp",EDGE,"E7");var subQ2=sQuery(id+"F0.wireOp",EDGE,"E6");var subQ3=sQuery(id+"F0.wireOp",EDGE,"E5");var subQ4=sQuery(id+"F0.wireOp",EDGE,"E4");var subQ5=sQuery(id+"F0.wireOp",EDGE,"E22.filletArc");var subQ6=sQuery(id+"F0.wireOp",EDGE,"E1.bottom");var subQ7=sQuery(id+"F0.wireOp",EDGE,"E1.right");var subQ8=sQuery(id+"F0.wireOp",EDGE,"E1.top");var subQ9=sQuery(id+"F0.wireOp",EDGE,"E1.left");var subQ10=sQuery(id+"F0.wireOp",EDGE,"E23.filletArc");var subQ11=sQuery(id+"F0.wireOp",EDGE,"E24.filletArc");Q0=makeQuery(id+"F2.boolean.opBoolean","SPLIT",FACE,{"disambiguationData":[TD([makeQuery(id+"F1.opExtrude","SWEPT_FACE",FACE,{"disambiguationData":[OSD([subQ6])]})])],"derivedFrom":makeQuery(id+"F1.opExtrude","CAP_FACE",FACE,{"disambiguationData":[OSD([subQ6,subQ8,subQ9,subQ7,subQ4,subQ3,subQ2,subQ1,subQ0,subQ5,subQ10,subQ11])],"isStart":true})});}
            var Q1;
            {var subQ0=sQuery(id+"F16.wireOp",EDGE,"E80");Q1=makeQuery(id+"F16.imprint","IMPRINT",FACE,{"disambiguationData":[TD([[makeQuery(id+"F16.imprint","IMPRINT",EDGE,{"derivedFrom":subQ0}),-1.0]])]});}
            var Q2;
            Q2=makeQuery(id+"F16.imprint","IMPRINT",FACE,{"disambiguationData":[TD([[makeQuery(id+"F16.imprint","IMPRINT",EDGE,{"derivedFrom":sQuery(id+"F16.wireOp",EDGE,"E88.MirrorC")}),1.0]])]});
            var Q3;
            Q3=makeQuery(id+"F2.opExtrude","CAP_FACE",FACE,{"disambiguationData":[OSD([sQuery(id+"F0.wireOp",EDGE,"E12"),sQuery(id+"F0.wireOp",EDGE,"E13"),sQuery(id+"F0.wireOp",EDGE,"E14"),sQuery(id+"F0.wireOp",EDGE,"E15"),sQuery(id+"F0.wireOp",EDGE,"E17.filletArc"),sQuery(id+"F0.wireOp",EDGE,"E18.filletArc"),sQuery(id+"F0.wireOp",EDGE,"E19.filletArc"),sQuery(id+"F0.wireOp",EDGE,"E20.filletArc"),sQuery(id+"F0.wireOp",EDGE,"E25.0"),sQuery(id+"F0.wireOp",EDGE,"E25.1"),sQuery(id+"F0.wireOp",EDGE,"E25.2"),sQuery(id+"F0.wireOp",EDGE,"E25.3"),sQuery(id+"F0.wireOp",EDGE,"E25.4"),sQuery(id+"F0.wireOp",EDGE,"E25.5"),sQuery(id+"F0.wireOp",EDGE,"E25.6"),sQuery(id+"F0.wireOp",EDGE,"E25.7")])],"isStart":false});
            extrude(context, id + "F17", {"entities" : qUnion([Q0, Q1, Q2]), "endBound" : BoundingType.UP_TO_SURFACE, "endBoundEntityFace" : qUnion([Q3]), "depth" : 25 * mm});
        }
    });
